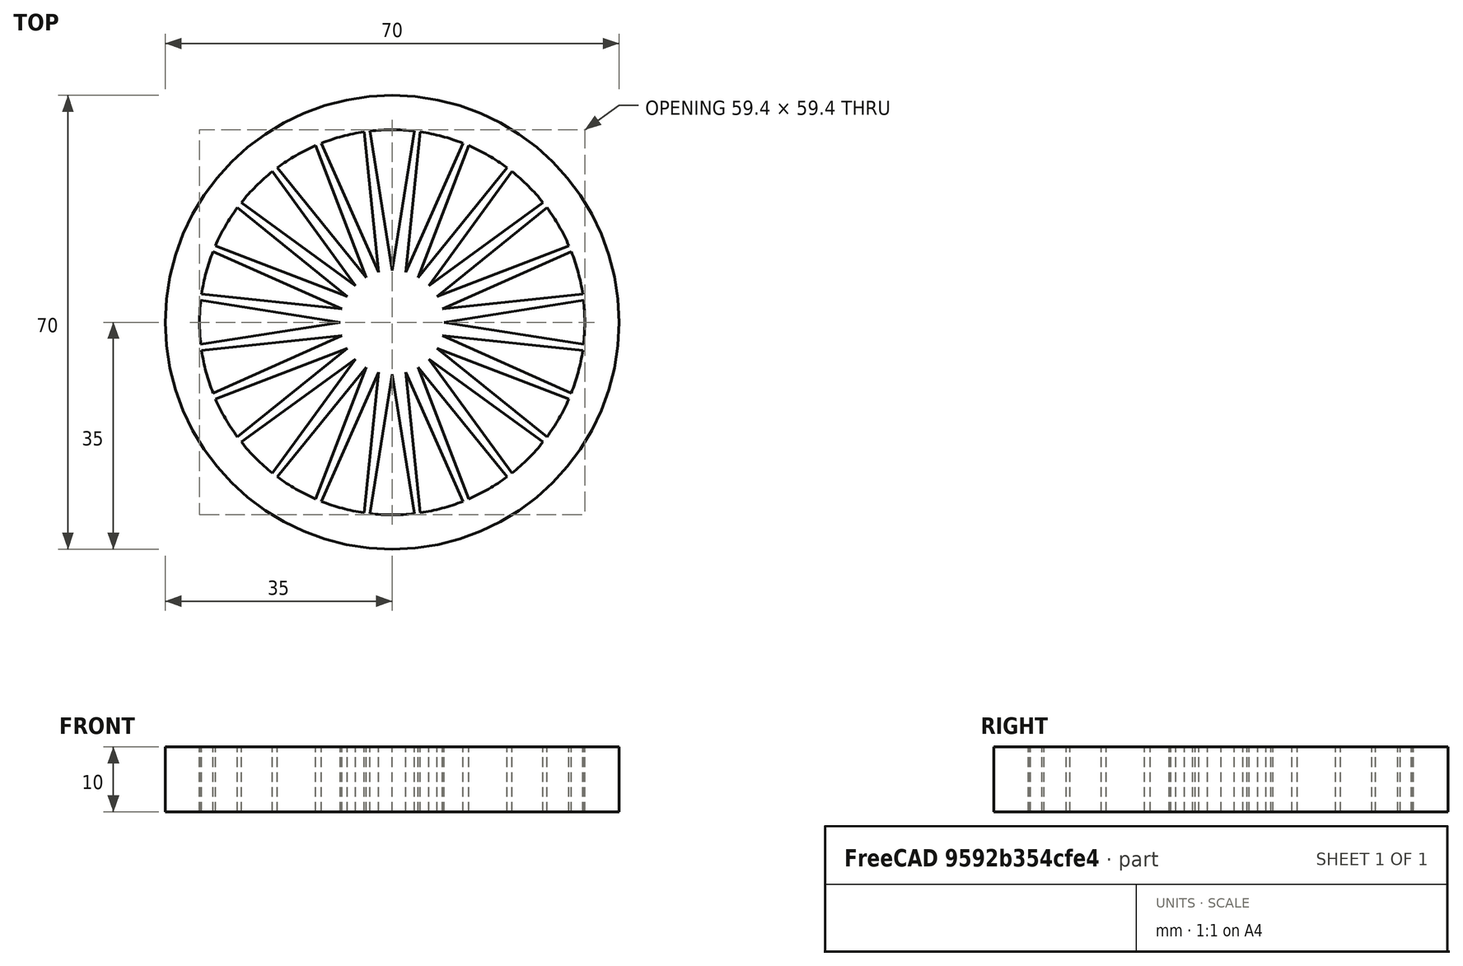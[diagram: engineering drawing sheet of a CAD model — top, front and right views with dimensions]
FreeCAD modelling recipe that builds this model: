
FCSTD DOCUMENT  (FreeCAD 0.16R6707 (Git))
Label: RuedaRadial
License: All rights reserved
LicenseURL: http://en.wikipedia.org/wiki/All_rights_reserved
objects: Part::Cylinder×4, Part::Cut×2, Part::FeaturePython×1, Spreadsheet::Sheet×1, Part::MultiFuse×1
note: 8 computed .brp shape members not serialized (recipe doc carries the construction recipe); baked Part::Feature solids carry a one-line shape summary decoded from their .brp

FEATURE [Part::Cylinder] Cylinder  label="CorteRadios"
  Angle = 360
  Height = 10
  Radius = 29.7
  expr: Height = Parametro.Height
  expr: Radius = Parametro.InternalRadius * Parametro.FactorCurvatura
FEATURE [Part::Cylinder] Cylinder001  label="Sector"
  Angle = 18
  Height = 10
  Placement = pos=(8,0,0) rot=(0,0,-1;0.15708rad)
  Radius = 22
  expr: Placement.Rotation.Angle = Sector.Angle / 2
  expr: Placement.Base.x = Parametro.CentralRadius
  expr: Height = Parametro.Height
  expr: Angle = 1.2 * 360 / Parametro.nSectores
  expr: Radius = Parametro.InternalRadius - Parametro.CentralRadius
FEATURE [Part::FeaturePython] Array  # Draft array (typed FeaturePython)
  Angle = 360
  ArrayType = 1
  Axis = (0,0,1)
  Base = -> Cylinder001
  Center = (0,0,0)
  Fuse = false
  IntervalAxis = (0,0,0)
  IntervalX = (1,0,0)
  IntervalY = (0,1,0)
  IntervalZ = (0,0,0)
  NumberPolar = 24
  NumberX = 2
  NumberY = 2
  NumberZ = 1
  expr: NumberPolar = Parametro.nSectores
FEATURE [Spreadsheet::Sheet] Spreadsheet  label="Parametro"
  cells = A1=Radio Interno; B1(InternalRadius)=30; A2=Alto; B2(Height)=10; A3=Radio Externo; B3(ExternalRadius)==35mm; A4=Radio Central; B4(CentralRadius)=8; A5=Nº Sectores; B5(nSectores)=24; A6=Factor Curvatura; B6(FactorCurvatura)=0.99
FEATURE [Part::Cut] Cut  label="Radios"
  Base = -> Cylinder
  Tool = -> Array
FEATURE [Part::Cylinder] Cylinder002  label="Borde externo Llanta"
  Angle = 360
  Height = 10
  Radius = 35
  expr: Radius = Parametro.ExternalRadius
  expr: Height = Parametro.Height
FEATURE [Part::Cylinder] Cylinder003  label="Borde Interno Llanta"
  Angle = 360
  Height = 10
  Radius = 29.7
  expr: Height = Parametro.Height
  expr: Radius = Parametro.FactorCurvatura * Parametro.InternalRadius
FEATURE [Part::Cut] Cut001  label="Llanta"
  Base = -> Cylinder002
  Tool = -> Cylinder003
FEATURE [Part::MultiFuse] Fusion  label="Rueda con radios"
  Shapes = -> [Cut,Cut001]
